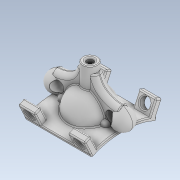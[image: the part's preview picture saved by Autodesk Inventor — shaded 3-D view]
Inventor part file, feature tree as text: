
AUTODESK INVENTOR PART (.ipt)
format: ipt  version: 2022 (Build 260153000, 153)  size: 1,428,480 bytes
history: native  units: in
note: dims shown in document units (in); Inventor stores cm internally (conversion verified against a paired STEP export)
features: fillet x20, sketch x13, extrude x10, mirror x9, revolve x4, plane x2
ambient origin geometry x8: Origin, YZ Plane, XZ Plane, XY Plane, X Axis, Y Axis, Z Axis, Center Point
bodies: Solid1 (feature_tree)
feature tree (58):
  extrude  "Extrusion1"  Depth=0.5906in
  extrude  "Extrusion9"  Depth=1.1024in TaperAngle=0.0deg
  plane  "Work Plane3"
  extrude  "Extrusion10"  Depth=0.2362in TaperAngle=0.0deg
  extrude  "Extrusion11"  Depth=0.2362in TaperAngle=0.0deg
  sketch  "Sketch18"  dims[d51=0.1654in d52=0.2362in d53=0.0in]
  sketch  "Sketch20"  dims[d57=0.1291in d58=0.6024in d59=0.0in]
  extrude  "Extrusion13"  Depth=0.6024in TaperAngle=0.0deg
  extrude  "Extrusion14"  Depth=0.3779in
  plane  "Work Plane5"
  sketch  "Sketch30"  dims[d60=0.1102in d61=0.0in d77=0.3779in]
  revolve  "Revolution9"  Angle=90.0deg
  mirror  "Mirror10"
  fillet  "Fillet22"  Radius=0.0197in
  mirror  "Mirror11"
  fillet  "Fillet23"  Radius=0.0118in
  mirror  "Mirror12"
  fillet  "Fillet24"  Radius=0.0118in
  fillet  "Fillet25"  Radius=0.0118in
  sketch  "Sketch37"  dims[d90=-0.1969in d94=90.0deg d115=0.0197in d116=0.0118in d117=0.0118in d118=0.0118in]
  revolve  "Revolution11"  Angle=165.0deg
  mirror  "Mirror14"
  mirror  "Mirror15"
  extrude  "Extrusion20"  Depth=0.5906in TaperAngle=0.0deg
  fillet  "Fillet28"  Radius=0.0039in
  mirror  "Mirror16"
  fillet  "Fillet29"  Radius=0.0039in
  extrude  "Extrusion21"  Depth=0.0787in
  mirror  "Mirror17"
  fillet  "Fillet30"  Radius=0.0197in
  fillet  "Fillet31"  Radius=0.0197in
  fillet  "Fillet32"  Radius=0.0157in
  fillet  "Fillet34"  Radius=0.0118in
  fillet  "Fillet35"  Radius=0.0276in
  fillet  "Fillet36"  [1 undecoded]
  revolve  "Revolution17"  [1 undecoded]
  mirror  "Mirror18"
  mirror  "Mirror19"
  revolve  "Revolution12"  [1 undecoded]
  fillet  "Fillet38"  Radius=0.248in
  extrude  "Extrusion25"  Depth=0.3937in TaperAngle=0.0deg
  extrude  "Extrusion26"  Depth=0.0256in
  fillet  "Fillet47"  Radius=0.0315in
  fillet  "Fillet48"  Radius=1.1681in
  fillet  "Fillet51"  Radius=0.0157in
  fillet  "Fillet52"  Radius=0.0157in
  fillet  "Fillet53"  Radius=0.0157in
  fillet  "Fillet54"  Radius=0.0197in
  fillet  "Fillet55"  Radius=0.0197in
  sketch  "Sketch2"  dims[d2=1.1024in d3=0.5906in]
  sketch  "Sketch15"  dims[d4=0.0866in d5=0.0in d43=1.1024in d44=0.0in]
  sketch  "Sketch17"  dims[d46=0.1102in d47=0.2362in d48=0.0197in d49=0.0in d50=0.0in]
  sketch  "Sketch38"  dims[d119=0.0197in d124=165.0deg]
  sketch  "Sketch39"  dims[d125=0.1693in d126=0.5906in d127=0.0in d129=0.0039in d130=0.0039in]
  sketch  "Sketch40"  dims[d131=0.5906in d132=0.0in d133=0.0787in d134=0.0197in d135=0.0197in d137=0.0157in d138=0.0118in d139=0.0276in d140=360.0deg]
  sketch  "Sketch50"  dims[d142=0.0197in d156=0.3779in]
  sketch  "Sketch51"  dims[d180=0.3779in d195=0.1142in d196=0.248in d197=0.0in]
  sketch  "Sketch52"  dims[d198=0.0472in d199=0.3937in d200=0.0in d201=0.0787in d202=0.0315in d206=1.1681in d207=0.0157in d208=0.0157in d209=0.0157in d210=0.0197in d211=0.0197in d212=0.0256in]
note: 3 required parameter values undecoded (feature->parameter linkage not recoverable at this tier; creation-order binding heuristic only, values carry confidence <= 0.55)